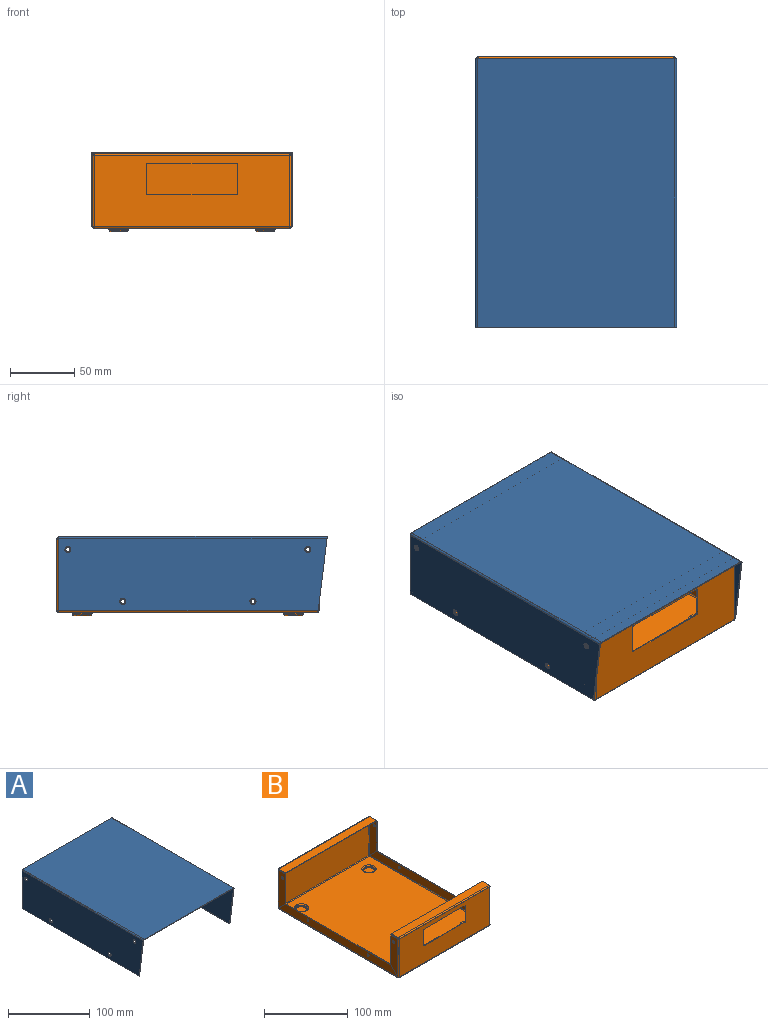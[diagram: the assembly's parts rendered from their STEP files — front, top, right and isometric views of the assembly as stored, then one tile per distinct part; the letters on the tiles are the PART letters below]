
ASSEMBLY  parts=2 mates=2
PART A: 30 faces, bbox 157.1x209.6x57.9 mm
  f0: plane 154.05x0.76mm, normal (0,-1,0), area 117.4mm2, adj f2,f3,f14,f27
  f1: plane 154.05x0.76mm, normal (0,1,0), area 117.4mm2, adj f2,f3,f13,f26
  f2: plane 209.55x154.05mm, normal (0,0,1), area 32281.4mm2, adj f0,f1,f15,f28
  f3: plane 209.55x154.05mm, normal (0,0,-1), area 32281.4mm2, adj f0,f1,f16,f29
  f4: plane 202.53x0.76mm, normal (0,0,-1), area 154.3mm2, adj f5,f10,f11,f12
  f5: plane 56.39x0.76mm, normal (0,1,0), area 43mm2, adj f4,f11,f12,f13
  f6: cylinder r=2.38mm len=4.76mm, axis (1,0,0), area 11.4mm2, adj f11,f12
  f7: cylinder r=2.38mm len=4.76mm, axis (1,0,0), area 11.4mm2, adj f11,f12
  f8: cylinder r=2.38mm len=4.76mm, axis (1,0,0), area 11.4mm2, adj f11,f12
  f9: cylinder r=2.38mm len=4.76mm, axis (1,0,0), area 11.4mm2, adj f11,f12
  f10: plane 56.39x6.92mm, normal (0,-0.99,-0.12), area 43.3mm2, adj f4,f11,f12,f14
  f11: plane 209.46x56.39mm, normal (1,0,0), area 11544.4mm2, adj f4,f5,f6,f7,f8,f9,f10,f15
  f12: plane 209.46x56.39mm, normal (-1,0,0), area 11544.4mm2, adj f4,f5,f6,f7,f8,f9,f10,f16
  f13: plane 1.52x1.52mm, normal (0,1,0), area 1.4mm2, adj f1,f5,f15,f16
  f14: bspline ~1.52x1.52mm, area 1.4mm2, adj f0,f10,f15,f16
  f15: cylinder r=1.52mm len=209.55mm, axis (0,1,0), area 501.5mm2, adj f2,f11,f13,f14
  f16: cylinder r=0.76mm len=209.55mm, axis (0,1,0), area 250.8mm2, adj f3,f12,f13,f14
  f17: plane 56.39x0.76mm, normal (0,1,0), area 43mm2, adj f18,f24,f25,f26
  f18: plane 202.53x0.76mm, normal (0,0,-1), area 154.3mm2, adj f17,f23,f24,f25
  f19: cylinder r=2.38mm len=4.76mm, axis (-1,0,0), area 11.4mm2, adj f24,f25
  f20: cylinder r=2.38mm len=4.76mm, axis (-1,0,0), area 11.4mm2, adj f24,f25
  f21: cylinder r=2.38mm len=4.76mm, axis (-1,0,0), area 11.4mm2, adj f24,f25
  f22: cylinder r=2.38mm len=4.76mm, axis (-1,0,0), area 11.4mm2, adj f24,f25
  f23: plane 56.39x6.92mm, normal (0,-0.99,-0.12), area 43.3mm2, adj f18,f24,f25,f27
  f24: plane 209.46x56.39mm, normal (-1,0,0), area 11544.4mm2, adj f17,f18,f19,f20,f21,f22,f23,f28
  f25: plane 209.46x56.39mm, normal (1,0,0), area 11544.4mm2, adj f17,f18,f19,f20,f21,f22,f23,f29
  f26: plane 1.52x1.52mm, normal (0,1,0), area 1.4mm2, adj f1,f17,f28,f29
  f27: bspline ~1.52x1.52mm, area 1.4mm2, adj f0,f23,f28,f29
  f28: cylinder r=1.52mm len=209.55mm, axis (0,1,0), area 501.5mm2, adj f2,f24,f26,f27
  f29: cylinder r=0.76mm len=209.55mm, axis (0,1,0), area 250.8mm2, adj f3,f25,f26,f27
PART B: 146 faces, bbox 155.4x204.7x61.2 mm
  f0: plane 0.76x0.76mm, normal (0,-1,0), area 0.6mm2, adj f1,f5,f6,f111
  f1: plane 11.94x0.76mm, normal (-1,0,0), area 9.1mm2, adj f0,f2,f5,f6
  f2: plane 153.92x0.76mm, normal (0,1,0), area 117.3mm2, adj f1,f3,f5,f6
  f3: plane 11.94x0.76mm, normal (1,0,0), area 9.1mm2, adj f2,f4,f5,f6
  f4: plane 0.76x0.76mm, normal (0,-1,0), area 0.6mm2, adj f3,f5,f6,f110
  f5: plane 153.92x11.94mm, normal (0,0,-1), area 1837.5mm2, adj f0,f1,f2,f3,f4,f113
  f6: plane 153.92x11.94mm, normal (0,0,1), area 1837.5mm2, adj f0,f1,f2,f3,f4,f112
  f7: plane 0.76x0.02mm, normal (1,0,0), area 0mm2, adj f17,f18,f86,f96
  f8: plane 0.76x0.02mm, normal (-1,0,0), area 0mm2, adj f17,f18,f87,f107
  f9: cylinder r=1.19mm len=1.19mm, axis (0,1,0), area 1.4mm2, adj f10,f16,f17,f18
  f10: plane 69.22x0.76mm, normal (0,0,-1), area 52.7mm2, adj f9,f11,f17,f18
  f11: cylinder r=1.19mm len=1.19mm, axis (0,1,0), area 1.4mm2, adj f10,f12,f17,f18
  f12: plane 21.98x0.76mm, normal (1,0,0), area 16.8mm2, adj f11,f13,f17,f18
  f13: cylinder r=1.19mm len=1.19mm, axis (0,1,0), area 1.4mm2, adj f12,f14,f17,f18
  f14: plane 69.22x0.76mm, normal (0,0,1), area 52.7mm2, adj f13,f15,f17,f18
  f15: cylinder r=1.19mm len=1.19mm, axis (0,1,0), area 1.4mm2, adj f14,f16,f17,f18
  f16: plane 21.98x0.76mm, normal (-1,0,0), area 16.8mm2, adj f9,f15,f17,f18
  f17: plane 152.4x55.63mm, normal (0,1,0), area 6734.2mm2, adj f7,f8,f9,f10,f11,f12,f13,f14
  f18: plane 152.4x55.63mm, normal (0,-1,0), area 6734.2mm2, adj f7,f8,f9,f10,f11,f12,f13,f14
  f19: plane 0.76x0.02mm, normal (-1,0,0), area 0mm2, adj f23,f24,f82,f87
  f20: plane 0.76x0.02mm, normal (1,0,0), area 0mm2, adj f23,f24,f60,f71
  f21: plane 0.76x0.02mm, normal (-1,0,0), area 0mm2, adj f23,f24,f61,f83
  f22: plane 0.76x0.02mm, normal (1,0,0), area 0mm2, adj f23,f24,f72,f86
  f23: plane 201.68x152.4mm, normal (0,0,1), area 29839.7mm2, adj f19,f20,f21,f22,f63,f74,f85,f89
  f24: plane 201.68x152.4mm, normal (0,0,-1), area 29839.7mm2, adj f19,f20,f21,f22,f62,f73,f84,f88
  f25: plane 0.76x0.76mm, normal (0,1,0), area 0.6mm2, adj f28,f30,f31,f56
  f26: plane 11.94x0.76mm, normal (-1,0,0), area 9.1mm2, adj f27,f29,f30,f31
  f27: plane 0.76x0.76mm, normal (0,1,0), area 0.6mm2, adj f26,f30,f31,f57
  f28: plane 11.94x0.76mm, normal (1,0,0), area 9.1mm2, adj f25,f29,f30,f31
  f29: plane 153.92x0.76mm, normal (0,-1,0), area 117.3mm2, adj f26,f28,f30,f31
  f30: plane 153.92x11.94mm, normal (0,0,-1), area 1837.5mm2, adj f25,f26,f27,f28,f29,f59
  f31: plane 153.92x11.94mm, normal (0,0,1), area 1837.5mm2, adj f25,f26,f27,f28,f29,f58
  f32: plane 0.76x0.02mm, normal (-1,0,0), area 0mm2, adj f34,f35,f52,f61
  f33: plane 0.76x0.02mm, normal (1,0,0), area 0mm2, adj f34,f35,f43,f60
  f34: plane 152.4x55.63mm, normal (0,-1,0), area 8477.4mm2, adj f32,f33,f45,f55,f59,f63
  f35: plane 152.4x55.63mm, normal (0,1,0), area 8477.4mm2, adj f32,f33,f44,f54,f58,f62
  f36: plane 11.94x0.76mm, normal (0,0,1), area 9.1mm2, adj f39,f40,f41,f42
  f37: plane 11.94x11.94mm, normal (0,-0.71,-0.71), area 12.9mm2, adj f39,f40,f41,f43
  f38: cylinder r=1.59mm len=3.18mm, axis (-1,0,0), area 7.6mm2, adj f40,f41
  f39: plane 43.67x0.76mm, normal (0,-1,0), area 33.3mm2, adj f36,f37,f40,f41
  f40: plane 55.61x11.94mm, normal (-1,0,0), area 584.7mm2, adj f36,f37,f38,f39,f45
  f41: plane 55.61x11.94mm, normal (1,0,0), area 584.7mm2, adj f36,f37,f38,f39,f44
  f42: plane 1.52x1.52mm, normal (0,0,1), area 1.4mm2, adj f36,f44,f45,f56
  f43: plane 1.52x1.52mm, normal (0,0,-1), area 1.4mm2, adj f33,f37,f44,f45
  f44: cylinder r=1.52mm len=55.61mm, axis (0,0,1), area 133.1mm2, adj f35,f41,f42,f43
  f45: cylinder r=0.76mm len=55.61mm, axis (0,0,1), area 66.6mm2, adj f34,f40,f42,f43
  f46: plane 11.94x11.94mm, normal (0,-0.71,-0.71), area 12.9mm2, adj f49,f50,f51,f52
  f47: plane 11.94x0.76mm, normal (0,0,1), area 9.1mm2, adj f49,f50,f51,f53
  f48: cylinder r=1.59mm len=3.18mm, axis (1,0,0), area 7.6mm2, adj f50,f51
  f49: plane 43.67x0.76mm, normal (0,-1,0), area 33.3mm2, adj f46,f47,f50,f51
  f50: plane 55.61x11.94mm, normal (1,0,0), area 584.7mm2, adj f46,f47,f48,f49,f55
  f51: plane 55.61x11.94mm, normal (-1,0,0), area 584.7mm2, adj f46,f47,f48,f49,f54
  f52: plane 1.52x1.52mm, normal (0,0,-1), area 1.4mm2, adj f32,f46,f54,f55
  f53: plane 1.52x1.52mm, normal (0,0,1), area 1.4mm2, adj f47,f54,f55,f57
  f54: cylinder r=1.52mm len=55.61mm, axis (0,0,-1), area 133.1mm2, adj f35,f51,f52,f53
  f55: cylinder r=0.76mm len=55.61mm, axis (0,0,-1), area 66.6mm2, adj f34,f50,f52,f53
  f56: plane 1.52x1.52mm, normal (1,0,0), area 1.4mm2, adj f25,f42,f58,f59
  f57: plane 1.52x1.52mm, normal (-1,0,0), area 1.4mm2, adj f27,f53,f58,f59
  f58: cylinder r=1.52mm len=152.4mm, axis (1,0,0), area 364.8mm2, adj f31,f35,f56,f57
  f59: cylinder r=0.76mm len=152.4mm, axis (1,0,0), area 182.4mm2, adj f30,f34,f56,f57
  f60: plane 1.52x1.52mm, normal (1,0,0), area 1.4mm2, adj f20,f33,f62,f63
  f61: plane 1.52x1.52mm, normal (-1,0,0), area 1.4mm2, adj f21,f32,f62,f63
  f62: cylinder r=1.52mm len=152.4mm, axis (1,0,0), area 364.8mm2, adj f24,f35,f60,f61
  f63: cylinder r=0.76mm len=152.4mm, axis (1,0,0), area 182.4mm2, adj f23,f34,f60,f61
  f64: plane 11.94x11.94mm, normal (0,0.71,0.71), area 12.9mm2, adj f68,f69,f70,f71
  f65: plane 11.94x11.94mm, normal (0,-0.71,0.71), area 12.9mm2, adj f68,f69,f70,f72
  f66: cylinder r=1.59mm len=3.18mm, axis (-1,0,0), area 7.6mm2, adj f69,f70
  f67: cylinder r=1.59mm len=3.18mm, axis (-1,0,0), area 7.6mm2, adj f69,f70
  f68: plane 177.76x0.76mm, normal (0,0,1), area 135.5mm2, adj f64,f65,f69,f70
  f69: plane 201.64x11.94mm, normal (-1,0,0), area 2248.8mm2, adj f64,f65,f66,f67,f68,f74
  f70: plane 201.64x11.94mm, normal (1,0,0), area 2248.8mm2, adj f64,f65,f66,f67,f68,f73
  f71: plane 1.52x1.52mm, normal (0,1,0), area 1.4mm2, adj f20,f64,f73,f74
  f72: plane 1.52x1.52mm, normal (0,-1,0), area 1.4mm2, adj f22,f65,f73,f74
  f73: cylinder r=1.52mm len=201.64mm, axis (0,1,0), area 482.7mm2, adj f24,f70,f71,f72
  f74: cylinder r=0.76mm len=201.64mm, axis (0,1,0), area 241.4mm2, adj f23,f69,f71,f72
  f75: plane 11.94x11.94mm, normal (0,-0.71,0.71), area 12.9mm2, adj f79,f80,f81,f82
  f76: plane 11.94x11.94mm, normal (0,0.71,0.71), area 12.9mm2, adj f79,f80,f81,f83
  f77: cylinder r=1.59mm len=3.18mm, axis (1,0,0), area 7.6mm2, adj f80,f81
  f78: cylinder r=1.59mm len=3.18mm, axis (1,0,0), area 7.6mm2, adj f80,f81
  f79: plane 177.76x0.76mm, normal (0,0,1), area 135.5mm2, adj f75,f76,f80,f81
  f80: plane 201.64x11.94mm, normal (1,0,0), area 2248.8mm2, adj f75,f76,f77,f78,f79,f85
  f81: plane 201.64x11.94mm, normal (-1,0,0), area 2248.8mm2, adj f75,f76,f77,f78,f79,f84
  f82: plane 1.52x1.52mm, normal (0,-1,0), area 1.4mm2, adj f19,f75,f84,f85
  f83: plane 1.52x1.52mm, normal (0,1,0), area 1.4mm2, adj f21,f76,f84,f85
  f84: cylinder r=1.52mm len=201.64mm, axis (0,-1,0), area 482.7mm2, adj f24,f81,f82,f83
  f85: cylinder r=0.76mm len=201.64mm, axis (0,-1,0), area 241.4mm2, adj f23,f80,f82,f83
  f86: plane 1.52x1.52mm, normal (1,0,0), area 1.4mm2, adj f7,f22,f88,f89
  f87: plane 1.52x1.52mm, normal (-1,0,0), area 1.4mm2, adj f8,f19,f88,f89
  f88: cylinder r=1.52mm len=152.4mm, axis (1,0,0), area 364.8mm2, adj f18,f24,f86,f87
  f89: cylinder r=0.76mm len=152.4mm, axis (1,0,0), area 182.4mm2, adj f17,f23,f86,f87
  f90: plane 11.94x11.94mm, normal (0,0.71,-0.71), area 12.9mm2, adj f93,f94,f95,f96
  f91: plane 11.94x0.76mm, normal (0,0,1), area 9.1mm2, adj f93,f94,f95,f97
  f92: cylinder r=1.59mm len=3.18mm, axis (-1,0,0), area 7.6mm2, adj f94,f95
  f93: plane 43.67x0.76mm, normal (0,1,0), area 33.3mm2, adj f90,f91,f94,f95
  f94: plane 55.61x11.94mm, normal (-1,0,0), area 584.7mm2, adj f90,f91,f92,f93,f99
  f95: plane 55.61x11.94mm, normal (1,0,0), area 584.7mm2, adj f90,f91,f92,f93,f98
  f96: plane 1.52x1.52mm, normal (0,0,-1), area 1.4mm2, adj f7,f90,f98,f99
  f97: plane 1.52x1.52mm, normal (0,0,1), area 1.4mm2, adj f91,f98,f99,f110
  f98: cylinder r=1.52mm len=55.61mm, axis (0,0,-1), area 133.1mm2, adj f18,f95,f96,f97
  f99: cylinder r=0.76mm len=55.61mm, axis (0,0,-1), area 66.6mm2, adj f17,f94,f96,f97
  f100: plane 11.94x0.76mm, normal (0,0,1), area 9.1mm2, adj f103,f104,f105,f106
  f101: plane 11.94x11.94mm, normal (0,0.71,-0.71), area 12.9mm2, adj f103,f104,f105,f107
  f102: cylinder r=1.59mm len=3.18mm, axis (1,0,0), area 7.6mm2, adj f104,f105
  f103: plane 43.67x0.76mm, normal (0,1,0), area 33.3mm2, adj f100,f101,f104,f105
  f104: plane 55.61x11.94mm, normal (1,0,0), area 584.7mm2, adj f100,f101,f102,f103,f109
  f105: plane 55.61x11.94mm, normal (-1,0,0), area 584.7mm2, adj f100,f101,f102,f103,f108
  f106: plane 1.52x1.52mm, normal (0,0,1), area 1.4mm2, adj f100,f108,f109,f111
  f107: plane 1.52x1.52mm, normal (0,0,-1), area 1.4mm2, adj f8,f101,f108,f109
  f108: cylinder r=1.52mm len=55.61mm, axis (0,0,1), area 133.1mm2, adj f18,f105,f106,f107
  f109: cylinder r=0.76mm len=55.61mm, axis (0,0,1), area 66.6mm2, adj f17,f104,f106,f107
  f110: plane 1.52x1.52mm, normal (1,0,0), area 1.4mm2, adj f4,f97,f112,f113
  f111: plane 1.52x1.52mm, normal (-1,0,0), area 1.4mm2, adj f0,f106,f112,f113
  f112: cylinder r=1.52mm len=152.4mm, axis (1,0,0), area 364.8mm2, adj f6,f18,f110,f111
  f113: cylinder r=0.76mm len=152.4mm, axis (1,0,0), area 182.4mm2, adj f5,f17,f110,f111
  f114: cone r=7.94mm half-angle=10deg, axis (0,0,1), area 28.6mm2, adj f122,f129
  f115: plane 12.18x12.18mm, normal (0,0,-1), area 116.4mm2, adj f122
  f116: cone r=7.94mm half-angle=10deg, axis (0,0,1), area 28.6mm2, adj f125,f128
  f117: plane 12.18x12.18mm, normal (0,0,-1), area 116.4mm2, adj f125
  f118: cone r=7.94mm half-angle=10deg, axis (0,0,1), area 28.6mm2, adj f124,f127
  f119: plane 12.18x12.18mm, normal (0,0,-1), area 116.4mm2, adj f124
  f120: cone r=7.94mm half-angle=10deg, axis (0,0,1), area 28.6mm2, adj f123,f126
  f121: plane 12.18x12.18mm, normal (0,0,-1), area 116.4mm2, adj f123
  f122: torus R=6.09mm, axis (0,0,1), area 93.5mm2, adj f114,f115
  f123: torus R=6.09mm, axis (0,0,1), area 93.5mm2, adj f120,f121
  f124: torus R=6.09mm, axis (0,0,1), area 93.5mm2, adj f118,f119
  f125: torus R=6.09mm, axis (0,0,1), area 93.5mm2, adj f116,f117
  f126: torus R=8.44mm, axis (0,0,1), area 53.4mm2, adj f24,f120
  f127: torus R=8.44mm, axis (0,0,1), area 53.4mm2, adj f24,f118
  f128: torus R=8.44mm, axis (0,0,1), area 53.4mm2, adj f24,f116
  f129: torus R=8.44mm, axis (0,0,1), area 53.4mm2, adj f24,f114
  f130: torus R=8.44mm, axis (0,0,1), area 100.8mm2, adj f23,f133
  f131: torus R=6.09mm, axis (0,0,1), area 43.7mm2, adj f132,f133
  f132: plane 12.18x12.18mm, normal (0,0,1), area 116.4mm2, adj f131
  f133: cone r=7.19mm half-angle=10deg, axis (0,0,1), area 25.8mm2, adj f130,f131
  f134: torus R=8.44mm, axis (0,0,1), area 100.8mm2, adj f23,f137
  f135: torus R=6.09mm, axis (0,0,1), area 43.7mm2, adj f136,f137
  f136: plane 12.18x12.18mm, normal (0,0,1), area 116.4mm2, adj f135
  f137: cone r=7.19mm half-angle=10deg, axis (0,0,1), area 25.8mm2, adj f134,f135
  f138: torus R=8.44mm, axis (0,0,1), area 100.8mm2, adj f23,f141
  f139: torus R=6.09mm, axis (0,0,1), area 43.7mm2, adj f140,f141
  f140: plane 12.18x12.18mm, normal (0,0,1), area 116.4mm2, adj f139
  f141: cone r=7.19mm half-angle=10deg, axis (0,0,1), area 25.8mm2, adj f138,f139
  f142: cone r=7.19mm half-angle=10deg, axis (0,0,1), area 25.8mm2, adj f144,f145
  f143: plane 12.18x12.18mm, normal (0,0,1), area 116.4mm2, adj f144
  f144: torus R=6.09mm, axis (0,0,1), area 43.7mm2, adj f142,f143
  f145: torus R=8.44mm, axis (0,0,1), area 100.8mm2, adj f23,f142
PLACE A rot(axis=(0,0,1),0deg) t=(0,0,57.91)mm
PLACE B at identity fixed
MATE slider B.f92 <-> A.f9  axis (1,0,0) through (-76.96,-93.66,48.39)mm
MATE parallel A.f2 <-> B.f23  axis (0,0,1) through (0,-3.97,58.67)mm
